# Revit family: TESK_Насос вертикальный_TK200-250
name_source: partatom
category: Оборудование
units: mm (PartAtom-declared; Revit-internal decimal feet)

## family parameters
Всегда вертикально = Да
Классификация = Насос
На основе рабочей плоскости = Нет
Общий = Нет
При загрузке вырезать с полостями = Нет
Размер круглого соединителя = Использовать диаметр
Тип детали = Вставляется
Точка расчета площади = Нет

## types (29) — shared parameters
ADSK_URL документации изделия = https://teskpump.ru
ADSK_Единица измерения = шт.
ADSK_Завод-изготовитель = TESK
ADSK_Классификация нагрузок = Прочее
ADSK_Количество = 1
ADSK_Количество фаз = 3
ADSK_Количество фаз числовое = 3
ADSK_Коэффициент мощности = 1
ADSK_Напряжение = 400 В
URL = https://teskpump.ru
Изготовитель = TESK
Материал_1 = TESK_Черный_Условный
Материал_2 = TESK_Черный_Ребра_Условный
Плита_Толщина = 35 мм
Энергоэффективность = IE3

## per-type parameters (varying)
- ТК 200-15/4  18,5kW 3x380V 50Hz IE3: ADSK_Диаметр условный=200 мм; ADSK_Код изделия=55TK20015403380; ADSK_Масса=420; ADSK_Масса_Текст=420; ADSK_Наименование=Вертикальный насос TESK типа IN-LINE, DN200, Hmax=15м (3x380V 50Hz IE3); ADSK_Номинальная мощность=18.50 кВт; ADSK_Полная мощность=18.50 кВ·А; B1=360 мм; B2=280 мм; B3=278 мм; B4=219 мм; B5=360 мм; C=133 мм; D=350 мм; D2=250 мм; D3=338 мм; DN=200 мм; F0=340 мм; F1=266 мм; F2=133 мм; F3=213 мм; F4=252 мм; H1=270 мм; H2=343 мм; H3=1188 мм; H4=575 мм; L1=1000 мм; Напор максимальный=15; Плита_Глубина=404 мм; Плита_Ширина=404 мм
- ТК 200-18/4  22kW 3x380V 50Hz IE3: ADSK_Диаметр условный=200 мм; ADSK_Код изделия=55TK20018403380; ADSK_Масса=440; ADSK_Масса_Текст=440; ADSK_Наименование=Вертикальный насос TESK типа IN-LINE, DN200, Hmax=18м (3x380V 50Hz IE3); ADSK_Номинальная мощность=22.00 кВт; ADSK_Полная мощность=22.00 кВ·А; B1=360 мм; B2=280 мм; B3=278 мм; B4=219 мм; B5=360 мм; C=133 мм; D=350 мм; D2=250 мм; D3=338 мм; DN=200 мм; F0=340 мм; F1=266 мм; F2=133 мм; F3=213 мм; F4=252 мм; H1=270 мм; H2=343 мм; H3=1218 мм; H4=605 мм; L1=1000 мм; Напор максимальный=18; Плита_Глубина=404 мм; Плита_Ширина=404 мм
- ТК 200-24/4  30kW 3x380V 50Hz IE3: ADSK_Диаметр условный=200 мм; ADSK_Код изделия=55TK20024403380; ADSK_Масса=438; ADSK_Масса_Текст=438; ADSK_Наименование=Вертикальный насос TESK типа IN-LINE, DN200, Hmax=24м (3x380V 50Hz IE3); ADSK_Номинальная мощность=30.00 кВт; ADSK_Полная мощность=30.00 кВ·А; B1=400 мм; B2=305 мм; B3=303 мм; B4=252 мм; B5=360 мм; C=133 мм; D=400 мм; D2=275 мм; D3=404 мм; DN=200 мм; F0=340 мм; F1=266 мм; F2=133 мм; F3=213 мм; F4=252 мм; H1=270 мм; H2=343 мм; H3=1313 мм; H4=700 мм; L1=1100 мм; Напор максимальный=24; Плита_Глубина=404 мм; Плита_Ширина=404 мм
- ТК 200-30/4  37kW 3x380V 50Hz IE3: ADSK_Диаметр условный=200 мм; ADSK_Код изделия=55TK20030403380; ADSK_Масса=590; ADSK_Масса_Текст=590; ADSK_Наименование=Вертикальный насос TESK типа IN-LINE, DN200, Hmax=30м (3x380V 50Hz IE3); ADSK_Номинальная мощность=37.00 кВт; ADSK_Полная мощность=37.00 кВ·А; B1=450 мм; B2=335 мм; B3=303 мм; B4=252 мм; B5=360 мм; C=133 мм; D=450 мм; D2=305 мм; D3=404 мм; DN=200 мм; F0=340 мм; F1=266 мм; F2=133 мм; F3=213 мм; F4=252 мм; H1=270 мм; H2=373 мм; H3=1348 мм; H4=705 мм; L1=1100 мм; Напор максимальный=30; Плита_Глубина=404 мм; Плита_Ширина=404 мм
- ТК 200-35/4  45kW 3x380V 50Hz IE3: ADSK_Диаметр условный=200 мм; ADSK_Код изделия=55TK20035403380; ADSK_Масса=630; ADSK_Масса_Текст=630; ADSK_Наименование=Вертикальный насос TESK типа IN-LINE, DN200, Hmax=35м (3x380V 50Hz IE3); ADSK_Номинальная мощность=45.00 кВт; ADSK_Полная мощность=45.00 кВ·А; B1=450 мм; B2=335 мм; B3=303 мм; B4=252 мм; B5=360 мм; C=133 мм; D=450 мм; D2=305 мм; D3=404 мм; DN=200 мм; F0=340 мм; F1=266 мм; F2=133 мм; F3=213 мм; F4=252 мм; H1=270 мм; H2=373 мм; H3=1373 мм; H4=730 мм; L1=1100 мм; Напор максимальный=35; Плита_Глубина=404 мм; Плита_Ширина=404 мм
- ТК 200-44/4  55kW 3x380V 50Hz IE3: ADSK_Диаметр условный=200 мм; ADSK_Код изделия=55TK20044403380; ADSK_Масса=768; ADSK_Масса_Текст=768; ADSK_Наименование=Вертикальный насос TESK типа IN-LINE, DN200, Hmax=44м (3x380V 50Hz IE3); ADSK_Номинальная мощность=55.00 кВт; ADSK_Полная мощность=55.00 кВ·А; B1=490 мм; B2=370 мм; B3=315 мм; B4=269 мм; B5=360 мм; C=133 мм; D=550 мм; D2=340 мм; D3=438 мм; DN=200 мм; F0=340 мм; F1=266 мм; F2=133 мм; F3=213 мм; F4=252 мм; H1=270 мм; H2=388 мм; H3=1423 мм; H4=765 мм; L1=1100 мм; Напор максимальный=44; Плита_Глубина=404 мм; Плита_Ширина=404 мм
- ТК 200-53/4  75kW 3x380V 50Hz IE3: ADSK_Диаметр условный=200 мм; ADSK_Код изделия=55TK20053403380; ADSK_Масса=902; ADSK_Масса_Текст=902; ADSK_Наименование=Вертикальный насос TESK типа IN-LINE, DN200, Hmax=53м (3x380V 50Hz IE3); ADSK_Номинальная мощность=75.00 кВт; ADSK_Полная мощность=75.00 кВ·А; B1=550 мм; B2=410 мм; B3=315 мм; B4=269 мм; B5=360 мм; C=133 мм; D=550 мм; D2=380 мм; D3=438 мм; DN=200 мм; F0=340 мм; F1=266 мм; F2=133 мм; F3=213 мм; F4=252 мм; H1=270 мм; H2=388 мм; H3=1486 мм; H4=828 мм; L1=1100 мм; Напор максимальный=53; Плита_Глубина=404 мм; Плита_Ширина=404 мм
- ТК 200-12,5/4  22kW 3x380V 50Hz IE3: ADSK_Диаметр условный=200 мм; ADSK_Код изделия=55TK200125403380; ADSK_Масса=440; ADSK_Масса_Текст=440; ADSK_Наименование=Вертикальный насос TESK типа IN-LINE, DN200, Hmax=12.5м (3x380V 50Hz IE3); ADSK_Номинальная мощность=22.00 кВт; ADSK_Полная мощность=22.00 кВ·А; B1=360 мм; B2=280 мм; B3=278 мм; B4=219 мм; B5=360 мм; C=133 мм; D=350 мм; D2=250 мм; D3=338 мм; DN=200 мм; F0=340 мм; F1=266 мм; F2=133 мм; F3=213 мм; F4=252 мм; H1=270 мм; H2=343 мм; H3=1218 мм; H4=605 мм; L1=1000 мм; Напор максимальный=12.5; Плита_Глубина=404 мм; Плита_Ширина=404 мм
- ТК 200-20/4  30kW 3x380V 50Hz IE3: ADSK_Диаметр условный=200 мм; ADSK_Код изделия=55TK20020403380; ADSK_Масса=506; ADSK_Масса_Текст=506; ADSK_Наименование=Вертикальный насос TESK типа IN-LINE, DN200, Hmax=20м (3x380V 50Hz IE3); ADSK_Номинальная мощность=30.00 кВт; ADSK_Полная мощность=30.00 кВ·А; B1=400 мм; B2=305 мм; B3=278 мм; B4=219 мм; B5=360 мм; C=133 мм; D=400 мм; D2=275 мм; D3=338 мм; DN=200 мм; F0=340 мм; F1=266 мм; F2=133 мм; F3=213 мм; F4=252 мм; H1=270 мм; H2=343 мм; H3=1313 мм; H4=700 мм; L1=1000 мм; Напор максимальный=20; Плита_Глубина=404 мм; Плита_Ширина=404 мм
- ТК 200-23/4  37kW 3x380V 50Hz IE3: ADSK_Диаметр условный=200 мм; ADSK_Код изделия=55TK20023403380; ADSK_Масса=589; ADSK_Масса_Текст=589; ADSK_Наименование=Вертикальный насос TESK типа IN-LINE, DN200, Hmax=23м (3x380V 50Hz IE3); ADSK_Номинальная мощность=37.00 кВт; ADSK_Полная мощность=37.00 кВ·А; B1=450 мм; B2=335 мм; B3=303 мм; B4=252 мм; B5=360 мм; C=133 мм; D=450 мм; D2=305 мм; D3=404 мм; DN=200 мм; F0=340 мм; F1=266 мм; F2=133 мм; F3=213 мм; F4=252 мм; H1=270 мм; H2=373 мм; H3=1348 мм; H4=705 мм; L1=1100 мм; Напор максимальный=23; Плита_Глубина=404 мм; Плита_Ширина=404 мм
- ТК 200-27/4  45kW 3x380V 50Hz IE3: ADSK_Диаметр условный=200 мм; ADSK_Код изделия=55TK20027403380; ADSK_Масса=630; ADSK_Масса_Текст=630; ADSK_Наименование=Вертикальный насос TESK типа IN-LINE, DN200, Hmax=27м (3x380V 50Hz IE3); ADSK_Номинальная мощность=45.00 кВт; ADSK_Полная мощность=45.00 кВ·А; B1=450 мм; B2=335 мм; B3=303 мм; B4=252 мм; B5=360 мм; C=133 мм; D=450 мм; D2=305 мм; D3=404 мм; DN=200 мм; F0=340 мм; F1=266 мм; F2=133 мм; F3=213 мм; F4=252 мм; H1=270 мм; H2=373 мм; H3=1373 мм; H4=730 мм; L1=1100 мм; Напор максимальный=27; Плита_Глубина=404 мм; Плита_Ширина=404 мм
- ТК 200-32/4  55kW 3x380V 50Hz IE3: ADSK_Диаметр условный=200 мм; ADSK_Код изделия=55TK20032403380; ADSK_Масса=720; ADSK_Масса_Текст=720; ADSK_Наименование=Вертикальный насос TESK типа IN-LINE, DN200, Hmax=32м (3x380V 50Hz IE3); ADSK_Номинальная мощность=55.00 кВт; ADSK_Полная мощность=55.00 кВ·А; B1=490 мм; B2=370 мм; B3=303 мм; B4=252 мм; B5=360 мм; C=133 мм; D=550 мм; D2=340 мм; D3=404 мм; DN=200 мм; F0=340 мм; F1=266 мм; F2=133 мм; F3=213 мм; F4=252 мм; H1=270 мм; H2=373 мм; H3=1408 мм; H4=765 мм; L1=1100 мм; Напор максимальный=32; Плита_Глубина=404 мм; Плита_Ширина=404 мм
- ТК 200-43/4  75kW 3x380V 50Hz IE3: ADSK_Диаметр условный=200 мм; ADSK_Код изделия=55TK20043403380; ADSK_Масса=900; ADSK_Масса_Текст=900; ADSK_Наименование=Вертикальный насос TESK типа IN-LINE, DN200, Hmax=43м (3x380V 50Hz IE3); ADSK_Номинальная мощность=75.00 кВт; ADSK_Полная мощность=75.00 кВ·А; B1=550 мм; B2=410 мм; B3=315 мм; B4=269 мм; B5=360 мм; C=133 мм; D=550 мм; D2=380 мм; D3=438 мм; DN=200 мм; F0=340 мм; F1=266 мм; F2=133 мм; F3=213 мм; F4=252 мм; H1=270 мм; H2=388 мм; H3=1486 мм; H4=828 мм; L1=1100 мм; Напор максимальный=43; Плита_Глубина=404 мм; Плита_Ширина=404 мм
- ТК 200-50/4  90kW 3x380V 50Hz IE3: ADSK_Диаметр условный=200 мм; ADSK_Код изделия=55TK20050403380; ADSK_Масса=970; ADSK_Масса_Текст=970; ADSK_Наименование=Вертикальный насос TESK типа IN-LINE, DN200, Hmax=50м (3x380V 50Hz IE3); ADSK_Номинальная мощность=90.00 кВт; ADSK_Полная мощность=90.00 кВ·А; B1=550 мм; B2=410 мм; B3=315 мм; B4=269 мм; B5=360 мм; C=133 мм; D=550 мм; D2=380 мм; D3=438 мм; DN=200 мм; F0=340 мм; F1=266 мм; F2=133 мм; F3=213 мм; F4=252 мм; H1=270 мм; H2=388 мм; H3=1538 мм; H4=880 мм; L1=1100 мм; Напор максимальный=50; Плита_Глубина=404 мм; Плита_Ширина=404 мм
- ТК 250-15/4  30kW 3x380V 50Hz IE3: ADSK_Диаметр условный=250 мм; ADSK_Код изделия=55TK250125403380; ADSK_Масса=564; ADSK_Масса_Текст=564; ADSK_Наименование=Вертикальный насос TESK типа IN-LINE, DN250, Hmax=15м (3x380V 50Hz IE3); ADSK_Номинальная мощность=30.00 кВт; ADSK_Полная мощность=30.00 кВ·А; B1=400 мм; B2=305 мм; B3=316 мм; B4=243 мм; B5=390 мм; C=160 мм; D=400 мм; D2=275 мм; D3=386 мм; DN=250 мм; F0=405 мм; F1=319 мм; F2=160 мм; F3=253 мм; F4=300 мм; H1=300 мм; H2=393 мм; H3=1393 мм; H4=700 мм; L1=1100 мм; Напор максимальный=15; Плита_Глубина=434 мм; Плита_Ширина=434 мм
- ТК 250-18/4  37kW 3x380V 50Hz IE3: ADSK_Диаметр условный=250 мм; ADSK_Код изделия=55TK25014403380; ADSK_Масса=636; ADSK_Масса_Текст=636; ADSK_Наименование=Вертикальный насос TESK типа IN-LINE, DN250, Hmax=18м (3x380V 50Hz IE3); ADSK_Номинальная мощность=37.00 кВт; ADSK_Полная мощность=37.00 кВ·А; B1=450 мм; B2=335 мм; B3=316 мм; B4=243 мм; B5=390 мм; C=160 мм; D=450 мм; D2=305 мм; D3=386 мм; DN=250 мм; F0=405 мм; F1=319 мм; F2=160 мм; F3=253 мм; F4=300 мм; H1=300 мм; H2=423 мм; H3=1428 мм; H4=705 мм; L1=1100 мм; Напор максимальный=18; Плита_Глубина=434 мм; Плита_Ширина=434 мм
- ТК 250-21/4  45kW 3x380V 50Hz IE3: ADSK_Диаметр условный=250 мм; ADSK_Код изделия=55TK25015403380; ADSK_Масса=660; ADSK_Масса_Текст=660; ADSK_Наименование=Вертикальный насос TESK типа IN-LINE, DN250, Hmax=21м (3x380V 50Hz IE3); ADSK_Номинальная мощность=45.00 кВт; ADSK_Полная мощность=45.00 кВ·А; B1=450 мм; B2=335 мм; B3=316 мм; B4=243 мм; B5=390 мм; C=160 мм; D=450 мм; D2=305 мм; D3=386 мм; DN=250 мм; F0=405 мм; F1=319 мм; F2=160 мм; F3=253 мм; F4=300 мм; H1=300 мм; H2=423 мм; H3=1453 мм; H4=730 мм; L1=1100 мм; Напор максимальный=21; Плита_Глубина=434 мм; Плита_Ширина=434 мм
- ТК 250-27/4  55kW 3x380V 50Hz IE3: ADSK_Диаметр условный=250 мм; ADSK_Код изделия=55TK25017403380; ADSK_Масса=802; ADSK_Масса_Текст=802; ADSK_Наименование=Вертикальный насос TESK типа IN-LINE, DN250, Hmax=27м (3x380V 50Hz IE3); ADSK_Номинальная мощность=55.00 кВт; ADSK_Полная мощность=55.00 кВ·А; B1=490 мм; B2=365 мм; B3=329 мм; B4=264 мм; B5=440 мм; C=160 мм; D=550 мм; D2=335 мм; D3=428 мм; DN=250 мм; F0=405 мм; F1=319 мм; F2=160 мм; F3=253 мм; F4=300 мм; H1=300 мм; H2=438 мм; H3=1503 мм; H4=765 мм; L1=1100 мм; Напор максимальный=27; Плита_Глубина=484 мм; Плита_Ширина=484 мм
- ТК 250-36/4  75kW 3x380V 50Hz IE3: ADSK_Диаметр условный=250 мм; ADSK_Код изделия=55TK25018403380; ADSK_Масса=949; ADSK_Масса_Текст=949; ADSK_Наименование=Вертикальный насос TESK типа IN-LINE, DN250, Hmax=36м (3x380V 50Hz IE3); ADSK_Номинальная мощность=75.00 кВт; ADSK_Полная мощность=75.00 кВ·А; B1=550 мм; B2=370 мм; B3=329 мм; B4=264 мм; B5=440 мм; C=160 мм; D=550 мм; D2=340 мм; D3=428 мм; DN=250 мм; F0=405 мм; F1=319 мм; F2=160 мм; F3=253 мм; F4=300 мм; H1=300 мм; H2=438 мм; H3=1568 мм; H4=830 мм; L1=1100 мм; Напор максимальный=36; Плита_Глубина=484 мм; Плита_Ширина=484 мм
- ТК 250-44/4  90kW 3x380V 50Hz IE3: ADSK_Диаметр условный=250 мм; ADSK_Код изделия=55TK25020403380; ADSK_Масса=1065; ADSK_Масса_Текст=1065; ADSK_Наименование=Вертикальный насос TESK типа IN-LINE, DN250, Hmax=44м (3x380V 50Hz IE3); ADSK_Номинальная мощность=90.00 кВт; ADSK_Полная мощность=90.00 кВ·А; B1=550 мм; B2=410 мм; B3=347 мм; B4=292 мм; B5=440 мм; C=160 мм; D=550 мм; D2=380 мм; D3=484 мм; DN=250 мм; F0=405 мм; F1=319 мм; F2=160 мм; F3=253 мм; F4=300 мм; H1=305 мм; H2=461 мм; H3=1646 мм; H4=880 мм; L1=1200 мм; Напор максимальный=44; Плита_Глубина=484 мм; Плита_Ширина=484 мм
- ТК 250-53/4  110kW 3x380V 50Hz IE3: ADSK_Диаметр условный=250 мм; ADSK_Код изделия=55TK25021403380; ADSK_Масса=1292; ADSK_Масса_Текст=1292; ADSK_Наименование=Вертикальный насос TESK типа IN-LINE, DN250, Hmax=53м (3x380V 50Hz IE3); ADSK_Номинальная мощность=110.00 кВт; ADSK_Полная мощность=110.00 кВ·А; B1=625 мм; B2=530 мм; B3=347 мм; B4=292 мм; B5=440 мм; C=160 мм; D=660 мм; D2=500 мм; D3=484 мм; DN=250 мм; F0=405 мм; F1=319 мм; F2=160 мм; F3=253 мм; F4=300 мм; H1=305 мм; H2=461 мм; H3=1826 мм; H4=1060 мм; L1=1200 мм; Напор максимальный=53; Плита_Глубина=484 мм; Плита_Ширина=484 мм
- ТК 250-12,5/4  30kW 3x380V 50Hz IE3: ADSK_Диаметр условный=250 мм; ADSK_Код изделия=55TK25026403380; ADSK_Масса=563; ADSK_Масса_Текст=563; ADSK_Наименование=Вертикальный насос TESK типа IN-LINE, DN250, Hmax=12.5м (3x380V 50Hz IE3); ADSK_Номинальная мощность=30.00 кВт; ADSK_Полная мощность=30.00 кВ·А; B1=400 мм; B2=305 мм; B3=316 мм; B4=243 мм; B5=390 мм; C=160 мм; D=400 мм; D2=275 мм; D3=386 мм; DN=250 мм; F0=405 мм; F1=319 мм; F2=160 мм; F3=253 мм; F4=300 мм; H1=300 мм; H2=393 мм; H3=1393 мм; H4=700 мм; L1=1100 мм; Напор максимальный=12.5; Плита_Глубина=434 мм; Плита_Ширина=434 мм
- ТК 250-14/4  37kW 3x380V 50Hz IE3: ADSK_Диаметр условный=250 мм; ADSK_Код изделия=55TK25027403380; ADSK_Масса=635; ADSK_Масса_Текст=635; ADSK_Наименование=Вертикальный насос TESK типа IN-LINE, DN250, Hmax=14м (3x380V 50Hz IE3); ADSK_Номинальная мощность=37.00 кВт; ADSK_Полная мощность=37.00 кВ·А; B1=450 мм; B2=335 мм; B3=316 мм; B4=243 мм; B5=390 мм; C=160 мм; D=450 мм; D2=305 мм; D3=386 мм; DN=250 мм; F0=405 мм; F1=319 мм; F2=160 мм; F3=253 мм; F4=300 мм; H1=300 мм; H2=423 мм; H3=1428 мм; H4=705 мм; L1=1100 мм; Напор максимальный=14; Плита_Глубина=434 мм; Плита_Ширина=434 мм
- ТК 250-17/4  45kW 3x380V 50Hz IE3: ADSK_Диаметр условный=250 мм; ADSK_Код изделия=55TK25032403380; ADSK_Масса=659; ADSK_Масса_Текст=659; ADSK_Наименование=Вертикальный насос TESK типа IN-LINE, DN250, Hmax=17м (3x380V 50Hz IE3); ADSK_Номинальная мощность=45.00 кВт; ADSK_Полная мощность=45.00 кВ·А; B1=450 мм; B2=335 мм; B3=316 мм; B4=243 мм; B5=390 мм; C=160 мм; D=450 мм; D2=305 мм; D3=386 мм; DN=250 мм; F0=405 мм; F1=319 мм; F2=160 мм; F3=253 мм; F4=300 мм; H1=300 мм; H2=423 мм; H3=1453 мм; H4=730 мм; L1=1100 мм; Напор максимальный=17; Плита_Глубина=434 мм; Плита_Ширина=434 мм
- ТК 250-20/4  55kW 3x380V 50Hz IE3: ADSK_Диаметр условный=250 мм; ADSK_Код изделия=55TK25036403380; ADSK_Масса=759; ADSK_Масса_Текст=759; ADSK_Наименование=Вертикальный насос TESK типа IN-LINE, DN250, Hmax=20м (3x380V 50Hz IE3); ADSK_Номинальная мощность=55.00 кВт; ADSK_Полная мощность=55.00 кВ·А; B1=490 мм; B2=370 мм; B3=316 мм; B4=243 мм; B5=390 мм; C=160 мм; D=550 мм; D2=340 мм; D3=386 мм; DN=250 мм; F0=405 мм; F1=319 мм; F2=160 мм; F3=253 мм; F4=300 мм; H1=300 мм; H2=423 мм; H3=1503 мм; H4=780 мм; L1=1100 мм; Напор максимальный=20; Плита_Глубина=434 мм; Плита_Ширина=434 мм
- ТК 250-26/4  75kW 3x380V 50Hz IE3: ADSK_Диаметр условный=250 мм; ADSK_Код изделия=55TK25040403380; ADSK_Масса=948; ADSK_Масса_Текст=948; ADSK_Наименование=Вертикальный насос TESK типа IN-LINE, DN250, Hmax=26м (3x380V 50Hz IE3); ADSK_Номинальная мощность=75.00 кВт; ADSK_Полная мощность=75.00 кВ·А; B1=550 мм; B2=410 мм; B3=329 мм; B4=264 мм; B5=440 мм; C=160 мм; D=550 мм; D2=380 мм; D3=428 мм; DN=250 мм; F0=405 мм; F1=319 мм; F2=160 мм; F3=253 мм; F4=300 мм; H1=300 мм; H2=438 мм; H3=1568 мм; H4=830 мм; L1=1100 мм; Напор максимальный=26; Плита_Глубина=484 мм; Плита_Ширина=484 мм
- ТК 250-32/4  90kW 3x380V 50Hz IE3: ADSK_Диаметр условный=250 мм; ADSK_Код изделия=55TK25044403380; ADSK_Масса=1017; ADSK_Масса_Текст=1017; ADSK_Наименование=Вертикальный насос TESK типа IN-LINE, DN250, Hmax=32м (3x380V 50Hz IE3); ADSK_Номинальная мощность=90.00 кВт; ADSK_Полная мощность=90.00 кВ·А; B1=550 мм; B2=410 мм; B3=329 мм; B4=264 мм; B5=440 мм; C=160 мм; D=550 мм; D2=380 мм; D3=428 мм; DN=250 мм; F0=405 мм; F1=319 мм; F2=160 мм; F3=253 мм; F4=300 мм; H1=300 мм; H2=438 мм; H3=1618 мм; H4=880 мм; L1=1100 мм; Напор максимальный=32; Плита_Глубина=484 мм; Плита_Ширина=484 мм
- ТК 250-40/4  110kW 3x380V 50Hz IE3: ADSK_Диаметр условный=250 мм; ADSK_Код изделия=55TK25050403380; ADSK_Масса=1290; ADSK_Масса_Текст=1290; ADSK_Наименование=Вертикальный насос TESK типа IN-LINE, DN250, Hmax=40м (3x380V 50Hz IE3); ADSK_Номинальная мощность=110.00 кВт; ADSK_Полная мощность=110.00 кВ·А; B1=625 мм; B2=530 мм; B3=347 мм; B4=292 мм; B5=440 мм; C=160 мм; D=660 мм; D2=500 мм; D3=484 мм; DN=250 мм; F0=405 мм; F1=319 мм; F2=160 мм; F3=253 мм; F4=300 мм; H1=305 мм; H2=461 мм; H3=1826 мм; H4=1060 мм; L1=1200 мм; Напор максимальный=40; Плита_Глубина=484 мм; Плита_Ширина=484 мм
- ТК 250-50/4  132kW 3x380V 50Hz IE3: ADSK_Диаметр условный=250 мм; ADSK_Код изделия=55TK25053403380; ADSK_Масса=1400; ADSK_Масса_Текст=1400; ADSK_Наименование=Вертикальный насос TESK типа IN-LINE, DN250, Hmax=50м (3x380V 50Hz IE3); ADSK_Номинальная мощность=132.00 кВт; ADSK_Полная мощность=132.00 кВ·А; B1=625 мм; B2=530 мм; B3=347 мм; B4=292 мм; B5=440 мм; C=160 мм; D=660 мм; D2=500 мм; D3=484 мм; DN=250 мм; F0=405 мм; F1=319 мм; F2=160 мм; F3=253 мм; F4=300 мм; H1=305 мм; H2=461 мм; H3=1946 мм; H4=1180 мм; L1=1200 мм; Напор максимальный=50; Плита_Глубина=484 мм; Плита_Ширина=484 мм

note: column(s) folded — value = type name in every type: ADSK_Марка
